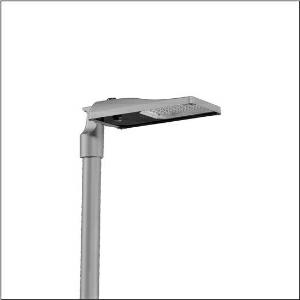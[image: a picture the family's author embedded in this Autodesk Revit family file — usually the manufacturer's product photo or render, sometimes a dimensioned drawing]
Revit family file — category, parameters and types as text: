
# Revit family: streetlight_sl_31_mini___st1_0a_5xh6d31t08ja_9cd4
name_source: partatom
category: Lighting Fixtures
units: mm (PartAtom-declared; Revit-internal decimal feet)

## family parameters
Cut with Voids When Loaded = No
Host = Face
Light Source = No
Part Type = Normal
Room Calculation Point = No
Round Connector Dimension = Use Diameter
Shared = No

## types (1)
- --- (1 x LED, 12270 lm, 82.5 W, 3000K)
    Apparent Load = 83 VA
    CIE Flux Codes = 40 73 97 100 100
    Color Rendering = 70
    Color Temperature = 3000K
    Default Elevation = 1800 mm
    Description = Streetlight SL 31 mini D4i, Desk-Remote mast luminaire for post-top, side-entry; light control with lens of PMMA; light distribution: ST1.0a, direct asymmetric distribution, for standard-compliant lighting for roads and squares; LED: luminous flux: 12.270lm, light colour: 730, colour temperature: 3000K; luminous efficacy: 148,7lm/W; control: pre-setting: logarithmic dimming characteristic, flexible luminous flux parameterisation, time-dependent luminous flux control, constant luminous flux control, power reduction, intelligent temperature release in ECG and LED module, overheat protection; luminaire housing, of diecast aluminium, Siteco® metallic grey (DB 702S), corrosivity category C5 high according to DIN EN ISO 12944; cover of toughened safety glass, transparent, opened without tools; mast flange of diecast aluminium, Siteco® metallic grey (DB 702S), spigot size: 76/60mm, mast flange included unmounted; with cable H07RN-F 2x 1.5mm², cable length: 10,5m, connection cable pre-assembled; mains connection: 220..240V, AC, 50/60Hz; power consumption (at start of service life): 82,5W / (at end of service life): 90,1W / (with reduced operation 50%): 36,8W; protection rating (complete): IP66; insulation class (complete): insulation class II (safety insulation); impact resistance: IK09; certification: CE, ENEC, ENEC+, VDE, UKCA, ZD4i; permissible operating ambient temperature for outdoor applications: -40..+50°C; packaging unit: 1 piece

Light Distribution: ST1.0a
    Height = 76 mm
    Lamp = 1 x LED
    Lamp Light Flux = 12270 lm
    Lamp Power = 82.5 W
    Lamp count = 1
    Length = 547 mm
    Luminous efficacy = 149 lm/W
    Manufacturer = Siteco
    ModVariant = No
    Model = 5XH6D31T08JA
    Number of Poles = 1
    OnlyDefault = Yes
    Power Factor = 1
    Product Name = Streetlight SL 31 mini | ST1.0a
    Product group = mast luminaire | pylon top
    ProductGroupID = 6100
    Protection Class = Protection class II
    Protection Degree = IP 66
    RLX_Detail_Level = 1
    RLX_Emergency_Light_Flux = 0 lm
    RLX_Emergency_Type = 0
    RLX_Emergency_Type_DB = No
    RlxData = <blob elided: 39881 chars, md5=e55c40d8>
    Socket = socket
    Standby Power = 0 W
    System Light Flux = 12270 lm
    System Power = 83 W
    Type Comments = factory setting: luminous flux: 100 % | dim-lin: 254 | 870 mA
    Type Image = l_1300332.jpg
    URL = http://relux.com
    VarID = @adj_050206
    Voltage = 0 V
    Weight = 0.00 kg
    Width = 265 mm

## geometry (parser evidence)
native form markers: Blend x4, Sweep x11
no freeform markers — native parametric forms only
